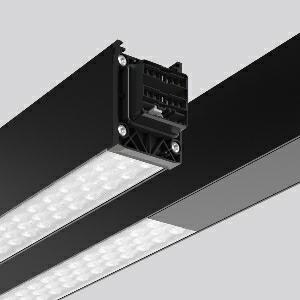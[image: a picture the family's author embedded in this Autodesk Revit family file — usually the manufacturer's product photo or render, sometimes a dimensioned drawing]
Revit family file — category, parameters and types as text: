
# Revit family: linedo_2_3m_30_1100_952330_843_476_504_7173
name_source: partatom
category: Lighting Fixtures
units: mm (PartAtom-declared; Revit-internal decimal feet)

## family parameters
Cut with Voids When Loaded = No
Host = Face
Light Source = No
Part Type = Normal
Room Calculation Point = No
Round Connector Dimension = Use Diameter
Shared = No

## types (1)
- LINEDO_2,3m_30_1100 (1 x LED Modul 840, 5200 lm, 4000)
    Apparent Load = 71 VA
    CIE Flux Codes = 89 97 99 100 100
    Color Rendering = 80
    Color Temperature = 4000
    Default Elevation = 1800 mm
    Description = LINEDO, 71 W, 10400 lm, 840, black, DALI
Continuous line luminaire, L 2291 B 58 H 76
    Height = 76 mm
    Lamp = 1 x LED Modul 840
    Lamp Light Flux = 5200 lm
    Lamp count = 1
    Length = 2291 mm
    Lifetime = 50000 h
    Luminous efficacy = 146 lm/W
    Manufacturer = RZB
    ModVariant = No
    Model = 952330.843.476.504
    Mounting Place = Ceiling
    Mounting Type = Surface mounted, Pendant
    Number of Poles = 1
    OnlyDefault = Yes
    Power Factor = 1
    Product Name = LINEDO_2,3m_30_1100
    Product group = Continuous line luminaire system Linedo IP 54
    ProductGroupID = 314
    Protection Class = Protection class I
    Protection Degree = IP 54
    RLX_Detail_Level = 1
    RLX_Emergency_Light_Flux = 0 lm
    RLX_Emergency_Type = 0
    RLX_Emergency_Type_DB = No
    RlxData = <blob elided: 56581 chars, md5=39e665ce>
    Socket = socket
    Standby Power = 0 W
    System Light Flux = 10400 lm
    System Power = 71 W
    Type Comments = Product without accessories
    Type Image = 954530.853.476.504.jpg
    URL = http://relux.com
    VarID = ---
    Voltage = 230 V
    Voltage Range = 220-240 V
    Weight = 0.00 kg
    Width = 58 mm

## geometry (parser evidence)
native form markers: Blend x4, Sweep x14
no freeform markers — native parametric forms only
